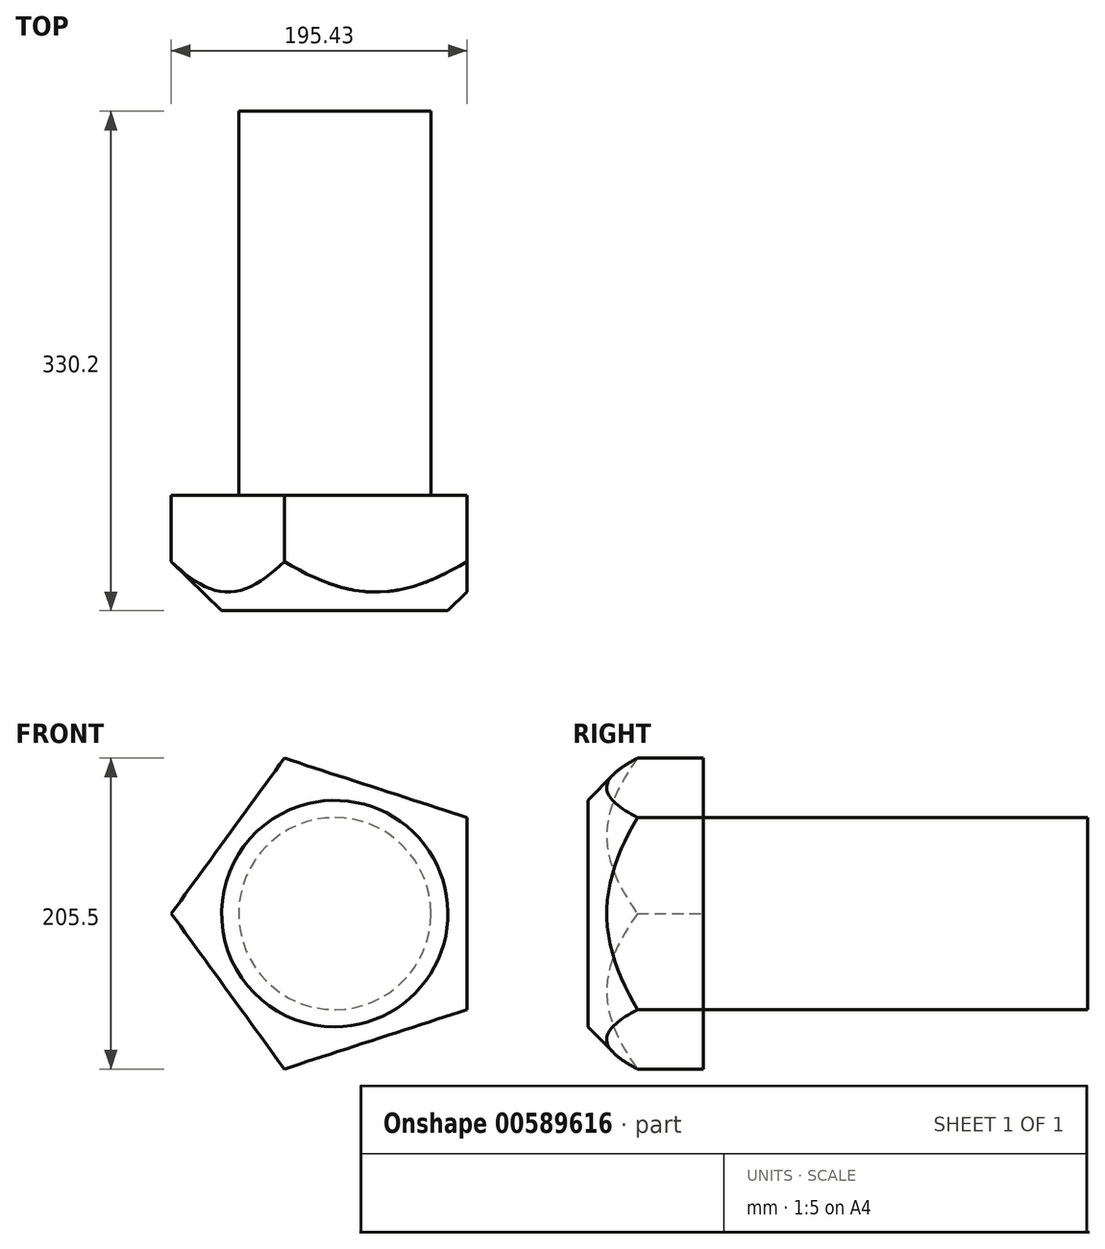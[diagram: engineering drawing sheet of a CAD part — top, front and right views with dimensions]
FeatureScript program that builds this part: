
annotation { "Feature Type Name" : "Feature", "Feature Type Description" : "" }
export const myFeature = defineFeature(function(context is Context, id is Id, definition is map)
    precondition{}
    {
        {
            var Q0;
            Q0=qCreatedBy(makeId("Front.planeOp"),FACE);
            var sketch = newSketch(context, id + "F0", { "sketchPlane" : qUnion([Q0])});
            skCircle(sketch, "E0", {"center": v(0, 0) * mm, "radius": 63.5 * mm});
            skSolve(sketch);
        }
        {
            var Q0;
            Q0=makeQuery(id+"F0.imprint","IMPRINT",FACE,{"disambiguationData":[TD([[makeQuery(id+"F0.imprint","IMPRINT",EDGE,{"derivedFrom":sQuery(id+"F0.wireOp",EDGE,"E0")}),1.0]])]});
            extrude(context, id + "F1", {"entities" : qUnion([Q0]), "endBound" : BoundingType.SYMMETRIC, "depth" : 254 * mm, "offsetDistance" : 25.4 * mm});
        }
        {
            var Q0;
            Q0=makeQuery(id+"F1.opExtrude","CAP_FACE",FACE,{"disambiguationData":[OSD([sQuery(id+"F0.wireOp",EDGE,"E0")])],"isStart":false});
            var sketch = newSketch(context, id + "F2", { "sketchPlane" : qUnion([Q0])});
            skCircle(sketch, "E1.cCircle", {"center": v(0, 0) * mm, "radius": 87.4 * mm, "construction": true});
            skLineSegment(sketch, "E1.0", {"start": v(87.4, 63.5) * mm, "end": v(87.4, -63.5) * mm});
            skLineSegment(sketch, "E1.1", {"start": v(87.4, -63.5) * mm, "end": v(-33.38, -102.75) * mm});
            skLineSegment(sketch, "E1.2", {"start": v(-33.38, -102.75) * mm, "end": v(-108.03, 0) * mm});
            skLineSegment(sketch, "E1.3", {"start": v(-108.03, 0) * mm, "end": v(-33.38, 102.75) * mm});
            skLineSegment(sketch, "E1.4", {"start": v(-33.38, 102.75) * mm, "end": v(87.4, 63.5) * mm});
            skPoint(sketch, "E1.0.midPoint", {"position": v(87.4, 0) * mm});
            skSolve(sketch);
        }
        {
            var Q0;
            Q0 = qSketchRegion(id + "F2", true);
            extrude(context, id + "F3", {"entities" : qUnion([Q0]), "operationType" : NewBodyOperationType.ADD, "depth" : 76.2 * mm, "offsetDistance" : 25.4 * mm});
        }
        {
            var Q0;
            Q0=qCreatedBy(makeId("Top.planeOp"),FACE);
            var sketch = newSketch(context, id + "F4", { "sketchPlane" : qUnion([Q0])});
            skLineSegment(sketch, "E2", {"start": v(66.7, -211.13) * mm, "end": v(178.57, -101.46) * mm});
            skLineSegment(sketch, "E3", {"start": v(178.57, -101.46) * mm, "end": v(178.57, -339.4) * mm});
            skLineSegment(sketch, "E4", {"start": v(178.57, -339.4) * mm, "end": v(66.7, -211.13) * mm});
            skLineSegment(sketch, "E5", {"start": v(0, 0) * mm, "end": v(0, -234.88) * mm});
            skSolve(sketch);
        }
        {
            var Q0;
            Q0=makeQuery(id+"F4.imprint","IMPRINT",FACE,{"disambiguationData":[TD([[makeQuery(id+"F4.imprint","IMPRINT",EDGE,{"derivedFrom":sQuery(id+"F4.wireOp",EDGE,"E2")}),-1.0]])]});
            var Q1;
            Q1=sQuery(id+"F4.wireOp",EDGE,"E5");
            revolve(context, id + "F5", {"operationType" : NewBodyOperationType.REMOVE, "entities" : qUnion([Q0]), "axis" : qUnion([Q1]), "revolveType" : RevolveType.FULL});
        }
    });
